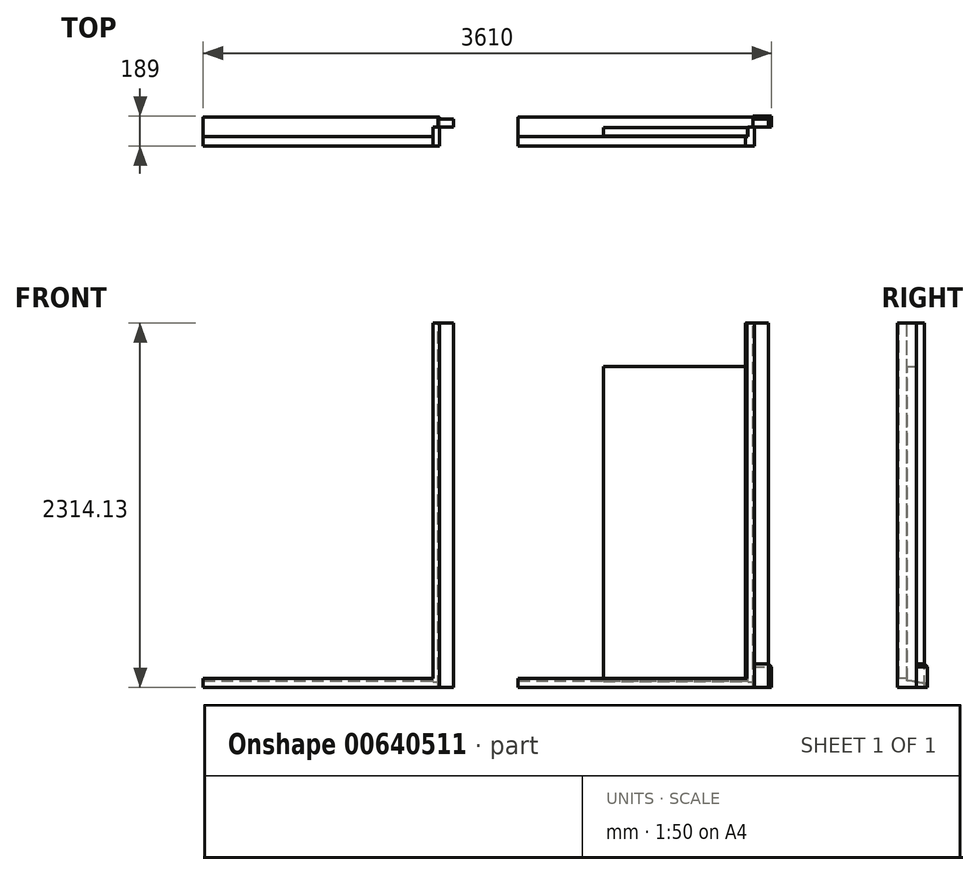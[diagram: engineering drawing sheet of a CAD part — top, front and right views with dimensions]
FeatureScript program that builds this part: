
annotation { "Feature Type Name" : "Feature", "Feature Type Description" : "" }
export const myFeature = defineFeature(function(context is Context, id is Id, definition is map)
    precondition{}
    {
        {
            var Q0;
            Q0=qCreatedBy(makeId("Right.planeOp"),FACE);
            var sketch = newSketch(context, id + "F0", { "sketchPlane" : qUnion([Q0])});
            skLineSegment(sketch, "E0.bottom", {"start": v(0, 0) * mm, "end": v(-183, 0) * mm});
            skLineSegment(sketch, "E0.top", {"start": v(-123, 57) * mm, "end": v(-183, 57) * mm});
            skLineSegment(sketch, "E0.left", {"start": v(0, 0) * mm, "end": v(0, 24) * mm});
            skLineSegment(sketch, "E0.right", {"start": v(-183, 0) * mm, "end": v(-183, 57) * mm});
            skLineSegment(sketch, "E1", {"start": v(0, 24) * mm, "end": v(-123, 42) * mm});
            skLineSegment(sketch, "E2", {"start": v(-123, 42) * mm, "end": v(-123, 57) * mm});
            skLineSegment(sketch, "E3", {"start": v(-183, 57) * mm, "end": v(-183, 161.9) * mm});
            skLineSegment(sketch, "E4", {"start": v(-64, 33.37) * mm, "end": v(-64, 167.06) * mm});
            skLineSegment(sketch, "E5", {"start": v(-65, 37.55) * mm, "end": v(-65, 2037.55) * mm});
            skLineSegment(sketch, "E6", {"start": v(-65, 2037.55) * mm, "end": v(-121, 2037.55) * mm});
            skLineSegment(sketch, "E7", {"start": v(-121, 2037.55) * mm, "end": v(-121, 45.75) * mm});
            skLineSegment(sketch, "E8", {"start": v(-65, 37.55) * mm, "end": v(-121, 45.75) * mm});
            skLineSegment(sketch, "E9", {"start": v(-183, 161.9) * mm, "end": v(-183, 2314.13) * mm});
            skLineSegment(sketch, "E10", {"start": v(-183, 2314.13) * mm, "end": v(-64, 2314.13) * mm});
            skLineSegment(sketch, "E11", {"start": v(-64, 2314.13) * mm, "end": v(-64, 167.06) * mm});
            skSolve(sketch);
        }
        {
            var Q0;
            Q0=makeQuery(id+"F0.imprint","IMPRINT",FACE,{"disambiguationData":[TD([[makeQuery(id+"F0.imprint","IMPRINT",EDGE,{"derivedFrom":sQuery(id+"F0.wireOp",EDGE,"E0.bottom")}),-1.0]])]});
            extrude(context, id + "F1", {"entities" : qUnion([Q0]), "oppositeDirection" : true, "depth" : 1500 * mm, "offsetDistance" : 25 * mm});
        }
        {
            var Q0;
            Q0=makeQuery(id+"F0.imprint","IMPRINT",FACE,{"disambiguationData":[TD([[makeQuery(id+"F0.imprint","IMPRINT",EDGE,{"derivedFrom":sQuery(id+"F0.wireOp",EDGE,"E5")}),1.0]])]});
            var Q1;
            Q1=makeQuery(id+"F0.imprint","IMPRINT",FACE,{"disambiguationData":[TD([[makeQuery(id+"F0.imprint","IMPRINT",EDGE,{"derivedFrom":sQuery(id+"F0.wireOp",EDGE,"E0.top")}),-1.0]])]});
            extrude(context, id + "F2", {"entities" : qUnion([Q0, Q1]), "operationType" : NewBodyOperationType.ADD, "oppositeDirection" : true, "depth" : 56 * mm, "offsetDistance" : 25 * mm});
        }
        {
            var Q0;
            Q0=makeQuery(id+"F2.opExtrude","CAP_FACE",FACE,{"disambiguationData":[OSD([sQuery(id+"F0.wireOp",EDGE,"E0.top"),sQuery(id+"F0.wireOp",EDGE,"E1"),sQuery(id+"F0.wireOp",EDGE,"E2"),sQuery(id+"F0.wireOp",EDGE,"E3"),sQuery(id+"F0.wireOp",EDGE,"E4"),sQuery(id+"F0.wireOp",EDGE,"E9"),sQuery(id+"F0.wireOp",EDGE,"E10"),sQuery(id+"F0.wireOp",EDGE,"E11")])],"isStart":false});
            var sketch = newSketch(context, id + "F3", { "sketchPlane" : qUnion([Q0])});
            skLineSegment(sketch, "E12", {"start": v(121, 45.52) * mm, "end": v(121, 2036.7) * mm});
            skLineSegment(sketch, "E13", {"start": v(121, 2036.7) * mm, "end": v(65, 2036.7) * mm});
            skLineSegment(sketch, "E14", {"start": v(65, 2036.7) * mm, "end": v(65, 37.6) * mm});
            skLineSegment(sketch, "E15", {"start": v(65, 37.6) * mm, "end": v(121, 45.52) * mm});
            skSolve(sketch);
        }
        {
            var Q0;
            Q0=makeQuery(id+"F3.imprint","IMPRINT",FACE,{"disambiguationData":[TD([[makeQuery(id+"F3.imprint","IMPRINT",EDGE,{"derivedFrom":sQuery(id+"F3.wireOp",EDGE,"E12")}),1.0]])]});
            extrude(context, id + "F4", {"entities" : qUnion([Q0]), "depth" : 3 * mm, "offsetDistance" : 25 * mm});
        }
        {
            var Q0;
            Q0=makeQuery(id+"F4.opExtrude","CAP_FACE",FACE,{"disambiguationData":[OSD([sQuery(id+"F3.wireOp",EDGE,"E12"),sQuery(id+"F3.wireOp",EDGE,"E13"),sQuery(id+"F3.wireOp",EDGE,"E14"),sQuery(id+"F3.wireOp",EDGE,"E15")])],"isStart":false});
            extrude(context, id + "F5", {"entities" : qUnion([Q0]), "depth" : 900 * mm, "offsetDistance" : 25 * mm});
        }
        {
            var Q0;
            Q0=makeQuery(id+"F2.opExtrude","SWEPT_FACE",FACE,{"disambiguationData":[OSD([sQuery(id+"F0.wireOp",EDGE,"E10")])]});
            var sketch = newSketch(context, id + "F6", { "sketchPlane" : qUnion([Q0])});
            skLineSegment(sketch, "E16.bottom", {"start": v(-10, -64) * mm, "end": v(90, -64) * mm});
            skLineSegment(sketch, "E16.top", {"start": v(-10, -14) * mm, "end": v(90, -14) * mm});
            skLineSegment(sketch, "E16.left", {"start": v(-10, -64) * mm, "end": v(-10, -14) * mm});
            skLineSegment(sketch, "E16.right", {"start": v(90, -64) * mm, "end": v(90, -14) * mm});
            skSolve(sketch);
        }
        {
            var Q0;
            Q0=makeQuery(id+"F6.imprint","IMPRINT",FACE,{"disambiguationData":[TD([[makeQuery(id+"F6.imprint","IMPRINT",EDGE,{"derivedFrom":sQuery(id+"F6.wireOp",EDGE,"E16.top")}),-1.0]])]});
            var Q1;
            Q1=makeQuery(id+"F1.opExtrude","SWEPT_FACE",FACE,{"disambiguationData":[OSD([sQuery(id+"F0.wireOp",EDGE,"E0.bottom")])]});
            extrude(context, id + "F7", {"entities" : qUnion([Q0]), "endBound" : BoundingType.UP_TO_SURFACE, "oppositeDirection" : true, "depth" : 25 * mm, "endBoundEntityFace" : qUnion([Q1]), "offsetDistance" : 25 * mm});
        }
        {
            var Q0;
            Q0=makeQuery(id+"F7.opExtrude","SWEPT_BODY",BODY,{"disambiguationData":[OSD([sQuery(id+"F6.wireOp",EDGE,"E16.bottom"),sQuery(id+"F6.wireOp",EDGE,"E16.top"),sQuery(id+"F6.wireOp",EDGE,"E16.left"),sQuery(id+"F6.wireOp",EDGE,"E16.right")])]});
            var Q1;
            Q1=makeQuery(id+"F1.opExtrude","SWEPT_BODY",BODY,{"disambiguationData":[OSD([sQuery(id+"F0.wireOp",EDGE,"E0.bottom"),sQuery(id+"F0.wireOp",EDGE,"E0.top"),sQuery(id+"F0.wireOp",EDGE,"E0.left"),sQuery(id+"F0.wireOp",EDGE,"E0.right"),sQuery(id+"F0.wireOp",EDGE,"E1"),sQuery(id+"F0.wireOp",EDGE,"E2")])]});
            var Q2;
            Q2=makeQuery(id+"F5.opExtrude","SWEPT_BODY",BODY,{"disambiguationData":[OSD([sQuery(id+"F3.wireOp",EDGE,"E12"),sQuery(id+"F3.wireOp",EDGE,"E13"),sQuery(id+"F3.wireOp",EDGE,"E14"),sQuery(id+"F3.wireOp",EDGE,"E15")])]});
            transform(context, id + "F8", {"entities" : qUnion([Q0, Q1, Q2]), "transformType" : TransformType.TRANSLATION_3D, "dx" : 2000 * mm, "dy" : 0 * mm, "dz" : 0 * mm, "makeCopy" : true});
        }
        {
            var Q0;
            Q0=makeQuery(id+"F8.opPattern","COPY",FACE,{"derivedFrom":makeQuery(id+"F7.opExtrude","CAP_FACE",FACE,{"disambiguationData":[OSD([sQuery(id+"F6.wireOp",EDGE,"E16.bottom"),sQuery(id+"F6.wireOp",EDGE,"E16.top"),sQuery(id+"F6.wireOp",EDGE,"E16.left"),sQuery(id+"F6.wireOp",EDGE,"E16.right")])],"isStart":false}),"instanceName":"1"});
            extrude(context, id + "F9", {"entities" : qUnion([Q0]), "operationType" : NewBodyOperationType.REMOVE, "oppositeDirection" : true, "depth" : 150 * mm, "offsetDistance" : 25 * mm});
        }
        {
            var Q0;
            Q0=makeQuery(id+"F9.boolean.opBoolean","COPY",FACE,{"derivedFrom":makeQuery(id+"F9.opExtrude","CAP_FACE",FACE,{"disambiguationData":[OSD([sQuery(id+"F6.wireOp",EDGE,"E16.bottom"),sQuery(id+"F6.wireOp",EDGE,"E16.top"),sQuery(id+"F6.wireOp",EDGE,"E16.left"),sQuery(id+"F6.wireOp",EDGE,"E16.right")])],"isStart":false})});
            var sketch = newSketch(context, id + "F10", { "sketchPlane" : qUnion([Q0])});
            skLineSegment(sketch, "E17.bottom", {"start": v(1990, 64) * mm, "end": v(2110, 64) * mm});
            skLineSegment(sketch, "E17.top", {"start": v(1990, -6) * mm, "end": v(2110, -6) * mm});
            skLineSegment(sketch, "E17.left", {"start": v(1990, 64) * mm, "end": v(1990, -6) * mm});
            skLineSegment(sketch, "E17.right", {"start": v(2110, 64) * mm, "end": v(2110, -6) * mm});
            skSolve(sketch);
        }
        {
            var Q0;
            {var subQ4=sQuery(id+"F10.wireOp",EDGE,"E17.top");Q0=makeQuery(id+"F10.imprint","IMPRINT",FACE,{"disambiguationData":[TD([[makeQuery(id+"F10.imprint","IMPRINT",EDGE,{"derivedFrom":subQ4}),1.0]])]});}
            var Q1;
            {var subQ4=makeQuery(id+"F9.boolean.opBoolean","COPY",EDGE,{"derivedFrom":makeQuery(id+"F9.opExtrude","CAP_EDGE",EDGE,{"disambiguationData":[OSD([sQuery(id+"F6.wireOp",EDGE,"E16.top")])],"isStart":false})});Q1=makeQuery(id+"F10.imprint","IMPRINT",FACE,{"disambiguationData":[TD([[makeQuery(id+"F10.imprint","IMPRINT",EDGE,{"derivedFrom":subQ4}),-1.0]])]});}
            extrude(context, id + "F11", {"entities" : qUnion([Q0, Q1]), "depth" : 150 * mm, "offsetDistance" : 25 * mm});
        }
        {
            var Q0;
            Q0=makeQuery(id+"F11.opExtrude","CAP_EDGE",EDGE,{"disambiguationData":[OSD([sQuery(id+"F10.wireOp",EDGE,"E17.top")])],"isStart":true});
            var Q1;
            Q1=makeQuery(id+"F11.opExtrude","CAP_EDGE",EDGE,{"disambiguationData":[OSD([sQuery(id+"F10.wireOp",EDGE,"E17.right")])],"isStart":true});
            chamfer(context, id + "F12", {"entities" : qUnion([Q0, Q1]), "width" : 20 * mm, "tangentPropagation" : true});
        }
        {
            var Q0;
            Q0=makeQuery(id+"F8.opPattern","COPY",EDGE,{"derivedFrom":makeQuery(id+"F1.opExtrude","SWEPT_EDGE",EDGE,{"disambiguationData":[OSD([sQuery(id+"F0.wireOp",EDGE,"E0.left"),sQuery(id+"F0.wireOp",EDGE,"E1")])]}),"instanceName":"1"});
            var Q1;
            Q1=makeQuery(id+"F1.opExtrude","SWEPT_EDGE",EDGE,{"disambiguationData":[OSD([sQuery(id+"F0.wireOp",EDGE,"E0.left"),sQuery(id+"F0.wireOp",EDGE,"E1")])]});
            fillet(context, id + "F13", {"entities" : qUnion([Q0, Q1]), "radius" : 5 * mm, "tangentPropagation" : true, "allowEdgeOverflow" : false});
        }
        {
            var Q0;
            Q0=makeQuery(id+"F2.opExtrude","CAP_FACE",FACE,{"disambiguationData":[OSD([sQuery(id+"F0.wireOp",EDGE,"E0.top"),sQuery(id+"F0.wireOp",EDGE,"E1"),sQuery(id+"F0.wireOp",EDGE,"E2"),sQuery(id+"F0.wireOp",EDGE,"E3"),sQuery(id+"F0.wireOp",EDGE,"E4"),sQuery(id+"F0.wireOp",EDGE,"E9"),sQuery(id+"F0.wireOp",EDGE,"E10"),sQuery(id+"F0.wireOp",EDGE,"E11")])],"isStart":false});
            extrude(context, id + "F14", {"entities" : qUnion([Q0]), "operationType" : NewBodyOperationType.REMOVE, "oppositeDirection" : true, "depth" : 15 * mm, "offsetDistance" : 25 * mm});
        }
        {
            var Q0;
            Q0=makeQuery(id+"F5.opExtrude","CAP_FACE",FACE,{"disambiguationData":[OSD([sQuery(id+"F3.wireOp",EDGE,"E12"),sQuery(id+"F3.wireOp",EDGE,"E13"),sQuery(id+"F3.wireOp",EDGE,"E14"),sQuery(id+"F3.wireOp",EDGE,"E15")])],"isStart":true});
            extrude(context, id + "F15", {"entities" : qUnion([Q0]), "operationType" : NewBodyOperationType.ADD, "depth" : 15 * mm, "offsetDistance" : 25 * mm});
        }
        {
            var Q0;
            Q0=makeQuery(id+"F8.opPattern","COPY",FACE,{"derivedFrom":makeQuery(id+"F2.opExtrude","CAP_FACE",FACE,{"disambiguationData":[OSD([sQuery(id+"F0.wireOp",EDGE,"E0.top"),sQuery(id+"F0.wireOp",EDGE,"E1"),sQuery(id+"F0.wireOp",EDGE,"E2"),sQuery(id+"F0.wireOp",EDGE,"E3"),sQuery(id+"F0.wireOp",EDGE,"E4"),sQuery(id+"F0.wireOp",EDGE,"E9"),sQuery(id+"F0.wireOp",EDGE,"E10"),sQuery(id+"F0.wireOp",EDGE,"E11")])],"isStart":false}),"instanceName":"1"});
            extrude(context, id + "F16", {"entities" : qUnion([Q0]), "operationType" : NewBodyOperationType.REMOVE, "oppositeDirection" : true, "depth" : 15 * mm, "offsetDistance" : 25 * mm});
        }
        {
            var Q0;
            Q0=makeQuery(id+"F8.opPattern","COPY",FACE,{"derivedFrom":makeQuery(id+"F5.opExtrude","CAP_FACE",FACE,{"disambiguationData":[OSD([sQuery(id+"F3.wireOp",EDGE,"E12"),sQuery(id+"F3.wireOp",EDGE,"E13"),sQuery(id+"F3.wireOp",EDGE,"E14"),sQuery(id+"F3.wireOp",EDGE,"E15")])],"isStart":true}),"instanceName":"1"});
            extrude(context, id + "F17", {"entities" : qUnion([Q0]), "operationType" : NewBodyOperationType.ADD, "depth" : 15 * mm, "offsetDistance" : 25 * mm});
        }
        {
            var Q0;
            Q0=makeQuery(id+"F8.opPattern","COPY",FACE,{"derivedFrom":makeQuery(id+"F2.opExtrude","SWEPT_FACE",FACE,{"disambiguationData":[OSD([sQuery(id+"F0.wireOp",EDGE,"E10")])]}),"instanceName":"1"});
            var sketch = newSketch(context, id + "F18", { "sketchPlane" : qUnion([Q0])});
            skLineSegment(sketch, "E18.bottom", {"start": v(1959, -183) * mm, "end": v(1951.5, -183) * mm});
            skLineSegment(sketch, "E18.top", {"start": v(1959, -123) * mm, "end": v(1944, -123) * mm});
            skLineSegment(sketch, "E18.left", {"start": v(1959, -183) * mm, "end": v(1959, -123) * mm});
            skLineSegment(sketch, "E18.right", {"start": v(1944, -175.5) * mm, "end": v(1944, -123) * mm});
            skLineSegment(sketch, "E19", {"start": v(1951.5, -183) * mm, "end": v(1951.5, -180.5) * mm});
            skLineSegment(sketch, "E20", {"start": v(1944, -175.5) * mm, "end": v(1946.5, -175.5) * mm});
            skArc(sketch, "E21", {"start": v(1946.5, -175.5) * mm, "mid": v(1947.96, -179.04) * mm, "end": v(1951.5, -180.5) * mm});
            skPoint(sketch, "E22.orphan", {"position": v(1944, -183) * mm});
            skSolve(sketch);
        }
        {
            var Q0;
            Q0=makeQuery(id+"F18.imprint","IMPRINT",FACE,{"disambiguationData":[TD([[makeQuery(id+"F18.imprint","IMPRINT",EDGE,{"derivedFrom":sQuery(id+"F18.wireOp",EDGE,"E18.bottom")}),-1.0]])]});
            var Q1;
            {var subQ0=sQuery(id+"F0.wireOp",EDGE,"E0.top");Q1=makeQuery(id+"F16.boolean.opBoolean","MERGE",FACE,{"derivedFrom":[makeQuery(id+"F8.opPattern","COPY",FACE,{"derivedFrom":makeQuery(id+"F1.opExtrude","SWEPT_FACE",FACE,{"disambiguationData":[OSD([subQ0])]}),"instanceName":"1"}),makeQuery(id+"F16.opExtrude","SWEPT_FACE",FACE,{"disambiguationData":[OSD([subQ0])]})]});}
            extrude(context, id + "F19", {"entities" : qUnion([Q0]), "operationType" : NewBodyOperationType.ADD, "endBound" : BoundingType.UP_TO_SURFACE, "oppositeDirection" : true, "depth" : 25 * mm, "endBoundEntityFace" : qUnion([Q1]), "offsetDistance" : 25 * mm});
        }
        {
            var Q0;
            Q0=makeQuery(id+"F4.opExtrude","SWEPT_BODY",BODY,{"disambiguationData":[OSD([sQuery(id+"F3.wireOp",EDGE,"E12"),sQuery(id+"F3.wireOp",EDGE,"E13"),sQuery(id+"F3.wireOp",EDGE,"E14"),sQuery(id+"F3.wireOp",EDGE,"E15")])]});
            deleteBodies(context, id + "F20", {"entities" : qUnion([Q0])});
        }
    });
